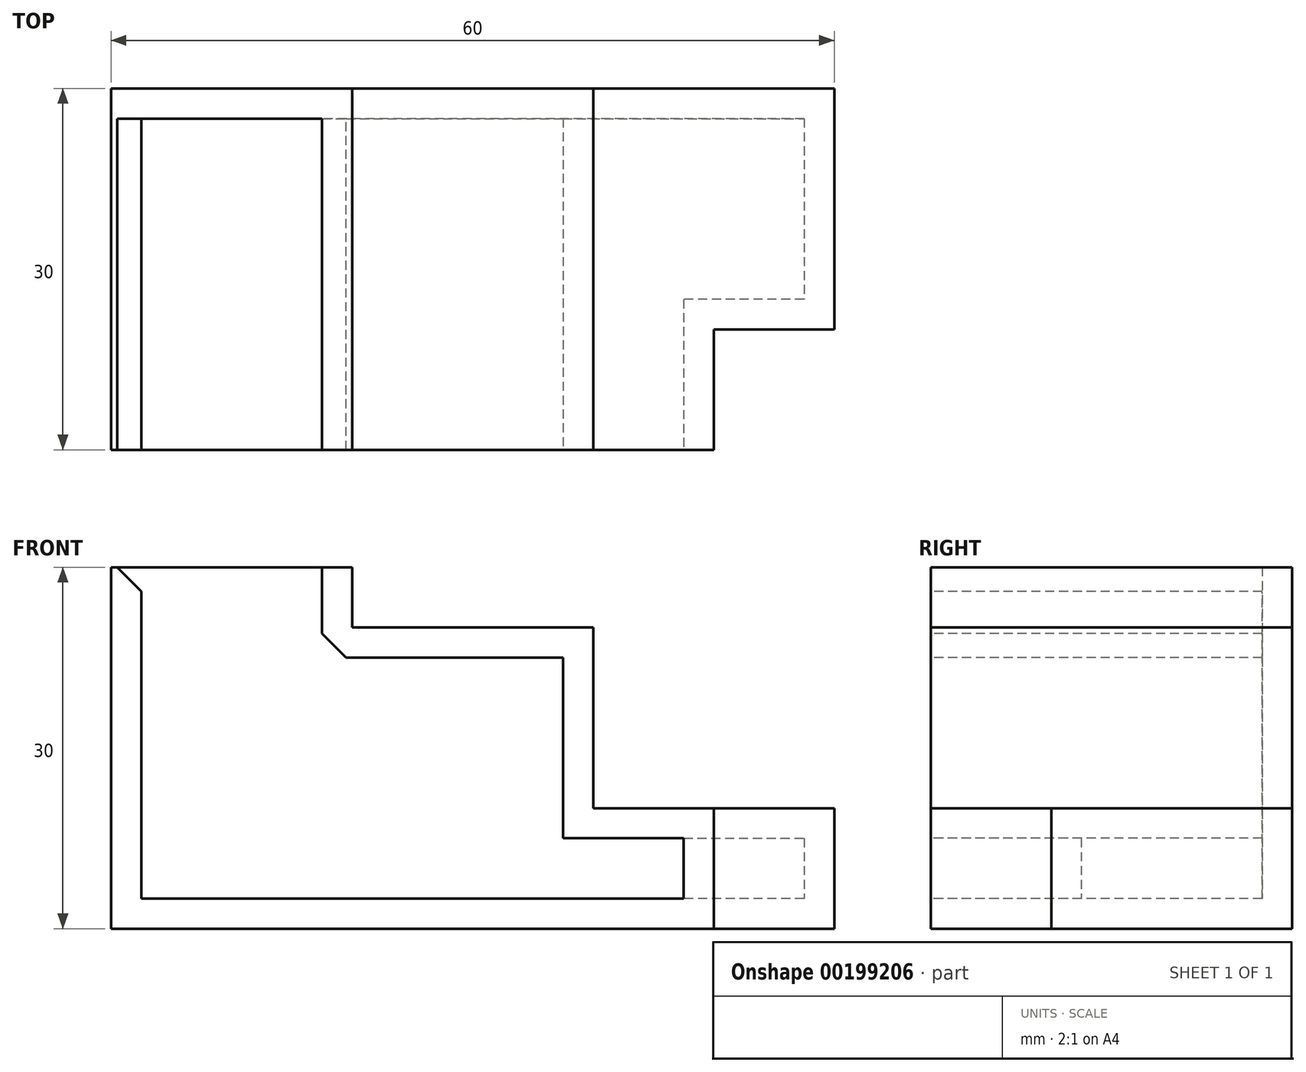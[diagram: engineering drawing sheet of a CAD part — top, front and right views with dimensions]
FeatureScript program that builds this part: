
annotation { "Feature Type Name" : "Feature", "Feature Type Description" : "" }
export const myFeature = defineFeature(function(context is Context, id is Id, definition is map)
    precondition{}
    {
        {
            var Q0;
            Q0=qCreatedBy(makeId("Front.planeOp"),FACE);
            var sketch = newSketch(context, id + "F0", { "sketchPlane" : qUnion([Q0])});
            skLineSegment(sketch, "E0", {"start": v(0, 0) * mm, "end": v(-60, 0) * mm});
            skLineSegment(sketch, "E1", {"start": v(-60, 0) * mm, "end": v(-60, 30) * mm});
            skLineSegment(sketch, "E2", {"start": v(-60, 30) * mm, "end": v(-40, 30) * mm});
            skLineSegment(sketch, "E3", {"start": v(-40, 30) * mm, "end": v(-40, 25) * mm});
            skLineSegment(sketch, "E4", {"start": v(-40, 25) * mm, "end": v(-20, 25) * mm});
            skLineSegment(sketch, "E5", {"start": v(-20, 25) * mm, "end": v(-20, 10) * mm});
            skLineSegment(sketch, "E6", {"start": v(-20, 10) * mm, "end": v(0, 10) * mm});
            skLineSegment(sketch, "E7", {"start": v(0, 10) * mm, "end": v(0, 0) * mm});
            skSolve(sketch);
        }
        {
            var Q0;
            Q0=makeQuery(id+"F0.imprint","IMPRINT",FACE,{"disambiguationData":[TD([[makeQuery(id+"F0.imprint","IMPRINT",EDGE,{"derivedFrom":sQuery(id+"F0.wireOp",EDGE,"E0")}),-1.0]])]});
            extrude(context, id + "F1", {"entities" : qUnion([Q0]), "oppositeDirection" : true, "depth" : 30 * mm});
        }
        {
            var Q0;
            Q0=makeQuery(id+"F1.opExtrude","CAP_FACE",FACE,{"disambiguationData":[OSD([sQuery(id+"F0.wireOp",EDGE,"E0"),sQuery(id+"F0.wireOp",EDGE,"E1"),sQuery(id+"F0.wireOp",EDGE,"E2"),sQuery(id+"F0.wireOp",EDGE,"E3"),sQuery(id+"F0.wireOp",EDGE,"E4"),sQuery(id+"F0.wireOp",EDGE,"E5"),sQuery(id+"F0.wireOp",EDGE,"E6"),sQuery(id+"F0.wireOp",EDGE,"E7")])],"isStart":true});
            var sketch = newSketch(context, id + "F2", { "sketchPlane" : qUnion([Q0])});
            skLineSegment(sketch, "E8.bottom", {"start": v(0, 0) * mm, "end": v(-10, 0) * mm});
            skLineSegment(sketch, "E8.top", {"start": v(0, 10) * mm, "end": v(-10, 10) * mm});
            skLineSegment(sketch, "E8.left", {"start": v(0, 0) * mm, "end": v(0, 10) * mm});
            skLineSegment(sketch, "E8.right", {"start": v(-10, 0) * mm, "end": v(-10, 10) * mm});
            skSolve(sketch);
        }
        {
            var Q0;
            Q0 = qSketchRegion(id + "F2", true);
            extrude(context, id + "F3", {"entities" : qUnion([Q0]), "operationType" : NewBodyOperationType.REMOVE, "oppositeDirection" : true, "depth" : 10 * mm});
        }
        {
            var Q0;
            Q0=makeQuery(id+"F1.opExtrude","SWEPT_FACE",FACE,{"disambiguationData":[OSD([sQuery(id+"F0.wireOp",EDGE,"E2")])]});
            var Q1;
            Q1=makeQuery(id+"F1.opExtrude","CAP_FACE",FACE,{"disambiguationData":[OSD([sQuery(id+"F0.wireOp",EDGE,"E0"),sQuery(id+"F0.wireOp",EDGE,"E1"),sQuery(id+"F0.wireOp",EDGE,"E2"),sQuery(id+"F0.wireOp",EDGE,"E3"),sQuery(id+"F0.wireOp",EDGE,"E4"),sQuery(id+"F0.wireOp",EDGE,"E5"),sQuery(id+"F0.wireOp",EDGE,"E6"),sQuery(id+"F0.wireOp",EDGE,"E7")])],"isStart":true});
            shell(context, id + "F4", {"entities" : qUnion([Q0, Q1]), "thickness" : 2.5 * mm});
        }
        {
            var Q0;
            Q0=makeQuery(id+"F4.opShell","OFFSET_EDGE",EDGE,{"disambiguationData":[OSD([sQuery(id+"F0.wireOp",EDGE,"E1"),sQuery(id+"F0.wireOp",EDGE,"E2")])]});
            chamfer(context, id + "F5", {"entities" : qUnion([Q0]), "width" : 2 * mm, "tangentPropagation" : true});
        }
        {
            var Q0;
            Q0=makeQuery(id+"F4.opShell","OFFSET_EDGE",EDGE,{"disambiguationData":[OSD([sQuery(id+"F0.wireOp",EDGE,"E3"),sQuery(id+"F0.wireOp",EDGE,"E4")])]});
            chamfer(context, id + "F6", {"entities" : qUnion([Q0]), "width" : 2 * mm, "tangentPropagation" : true});
        }
    });
